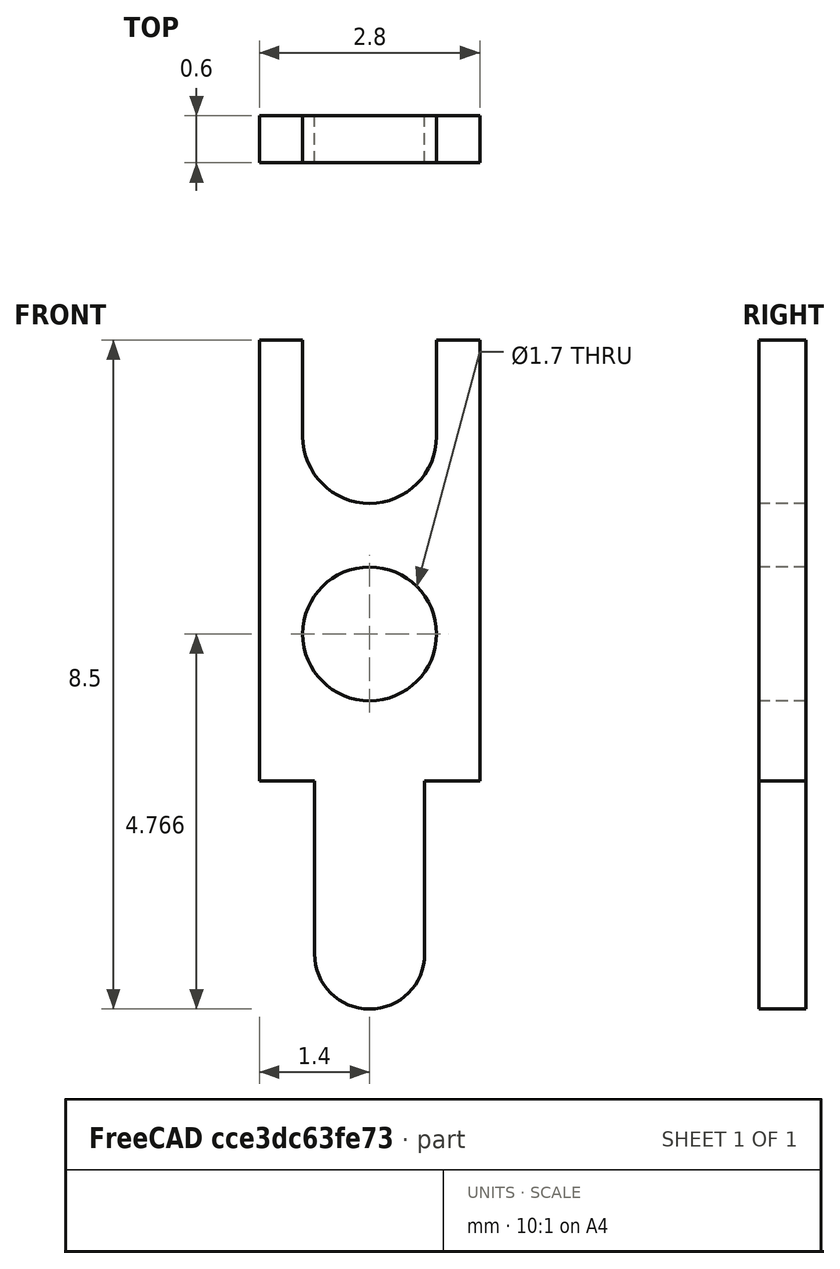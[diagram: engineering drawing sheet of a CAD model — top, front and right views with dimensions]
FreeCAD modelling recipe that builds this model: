
FCSTD DOCUMENT  (FreeCAD 0.17R12018 (Git))
Label: Pin_d1.4mm_L8.5mm_W2.8mm_FlatFork
License: All rights reserved
LicenseURL: http://en.wikipedia.org/wiki/All_rights_reserved
objects: Spreadsheet::Sheet×1, Sketcher::SketchObject×1, PartDesign::Pad×1, PartDesign::Body×1, App::Part×1
note: 4 computed .brp shape members not serialized (recipe doc carries the construction recipe); baked Part::Feature solids carry a one-line shape summary decoded from their .brp

FEATURE [Spreadsheet::Sheet] Spreadsheet  label="dimensions"
  cells = A1="L"; B1(L)=8.5; A2="Wtop"; B2(Wtop)=2.7999999999999998; A3="Wbottom"; B3(Wbottom)=1.3999999999999999; A4="Lbottom"; B4(Lbottom)=2.8999999999999999; A5="Wfork"; B5(Wfork)=1.7; A6="FractionFork"; B6(FractionFork)=0.25; A7="thick"; B7(thick)=0.59999999999999998
FEATURE [Sketcher::SketchObject] Sketch
  MapMode = 5
  Placement = pos=(0,0,0) rot=(0,0.707107,0.707107;3.14159rad)
  Support = -> [XZ_Plane001]
  expr: Constraints[44] = (dimensions.L - dimensions.Lbottom) * 0.66669999999999996
  expr: Constraints[43] = dimensions.Wfork / 2
  expr: Constraints[40] = dimensions.Wtop
  expr: Constraints[38] = dimensions.Wbottom
  expr: Constraints[39] = (dimensions.Wtop - dimensions.Wbottom) / 2
  expr: Constraints[37] = dimensions.Lbottom - dimensions.Wbottom / 2
  expr: Constraints[32] = dimensions.L - dimensions.Lbottom
  expr: Constraints[19] = dimensions.Wfork
  sketch-geometry (15):
    g0: LineSegment StartX=-1.4 StartY=5.6 StartZ=0 EndX=-1.4 EndY=0 EndZ=0
    g1: LineSegment StartX=-1.4 StartY=0 StartZ=0 EndX=-0.7 EndY=0 EndZ=0
    g2: LineSegment StartX=-0.7 StartY=0 StartZ=0 EndX=-0.7 EndY=-2.2 EndZ=0
    g3: LineSegment StartX=0.7 StartY=0 StartZ=0 EndX=0.7 EndY=-2.2 EndZ=0
    g4: LineSegment StartX=0.7 StartY=0 StartZ=0 EndX=1.4 EndY=0 EndZ=0
    g5: LineSegment StartX=1.4 StartY=0 StartZ=0 EndX=1.4 EndY=5.6 EndZ=0
    g6: LineSegment StartX=1.4 StartY=5.6 StartZ=0 EndX=0.85 EndY=5.6 EndZ=0
    g7: LineSegment StartX=0.85 StartY=5.6 StartZ=0 EndX=0.85 EndY=4.375 EndZ=0
    g8: LineSegment StartX=-0.85 StartY=4.375 StartZ=0 EndX=-0.85 EndY=5.6 EndZ=0
    g9: LineSegment StartX=-0.85 StartY=5.6 StartZ=0 EndX=-1.4 EndY=5.6 EndZ=0
    g10: ArcOfCircle CenterX=0 CenterY=-2.2 CenterZ=0 NormalX=0 NormalY=0 NormalZ=1 Radius=0.7 StartAngle=3.14159 EndAngle=6.28319
    g11: ArcOfCircle CenterX=0 CenterY=4.375 CenterZ=0 NormalX=0 NormalY=0 NormalZ=1 Radius=0.85 StartAngle=3.14159 EndAngle=6.28319
    g12: LineSegment [constr] StartX=-0.7 StartY=-2.2 StartZ=0 EndX=0.7 EndY=-2.2 EndZ=0
    g13: LineSegment [constr] StartX=-0.85 StartY=4.375 StartZ=0 EndX=0.85 EndY=4.375 EndZ=0
    g14: Circle CenterX=0 CenterY=1.86648 CenterZ=0 NormalX=0 NormalY=0 NormalZ=1 Radius=0.85
  constraints (45):
    c: PointOnObject(g3,g-1)
    c: Horizontal(g6)
    c: Vertical(g7)
    c: Vertical(g8)
    c: Coincident(g9,g0)
    c: Horizontal(g9)
    c: Equal(g9,g6)
    c: PointOnObject(g10,g-2)
    c: Coincident(g8,g9)
    c: Coincident(g6,g7)
    c: Coincident(g5,g6)
    c: Coincident(g11,g8)
    c: Coincident(g11,g7)
    c: Coincident(g12,g3)
    c: Coincident(g13,g8)
    c: Coincident(g13,g7)
    c: Horizontal(g13)
    c: PointOnObject(g11,g13)
    c: DistanceY(g8,g6) = 0
    c: DistanceX(g8,g6) = 1.7
    c: DistanceY(g8,g8) = 1.225
    c: Coincident(g12,g2)
    c: Coincident(g2,g10)
    c: Coincident(g3,g10)
    c: PointOnObject(g10,g12)
    c: Horizontal(g12)
    c: Vertical(g3)
    c: Vertical(g2)
    c: Horizontal(g1)
    c: Horizontal(g4)
    c: Vertical(g5)
    c: Vertical(g0)
    c: DistanceY(g5,g5) = 5.6
    c: Coincident(g5,g4)
    c: Coincident(g0,g1)
    c: Coincident(g4,g3)
    c: Coincident(g1,g2)
    c: DistanceY(g3,g3) = 2.2
    c: DistanceX(g2,g3) = 1.4
    c: DistanceX(g1,g1) = 0.7
    c: DistanceX(g0,g5) = 2.8
    c: PointOnObject(g1,g-1)
    c: PointOnObject(g14,g-2)
    c: Radius(g14) = 0.85
    c: DistanceY(g14,g8) = 3.73352
FEATURE [PartDesign::Pad] Pad  label="Pin_d1.4mm_L8.5mm_W2.8mm_FlatFork"
  Length = 0.6
  Length2 = 100
  Midplane = true
  Placement = pos=(0,0,0) rot=(1,0,0;1.5708rad)
  Profile = -> Sketch
  Type = 0
  expr: Length = dimensions.thick
FEATURE [PartDesign::Body] PadBody  label="Body"
  Group = -> [Sketch,Pad]
  Origin = -> Origin001
  Tip = -> Pad
FEATURE [App::Part] Part
  Group = -> [PadBody]
  License = CC BY 3.0
  LicenseURL = http://creativecommons.org/licenses/by/3.0/
  Origin = -> Origin
